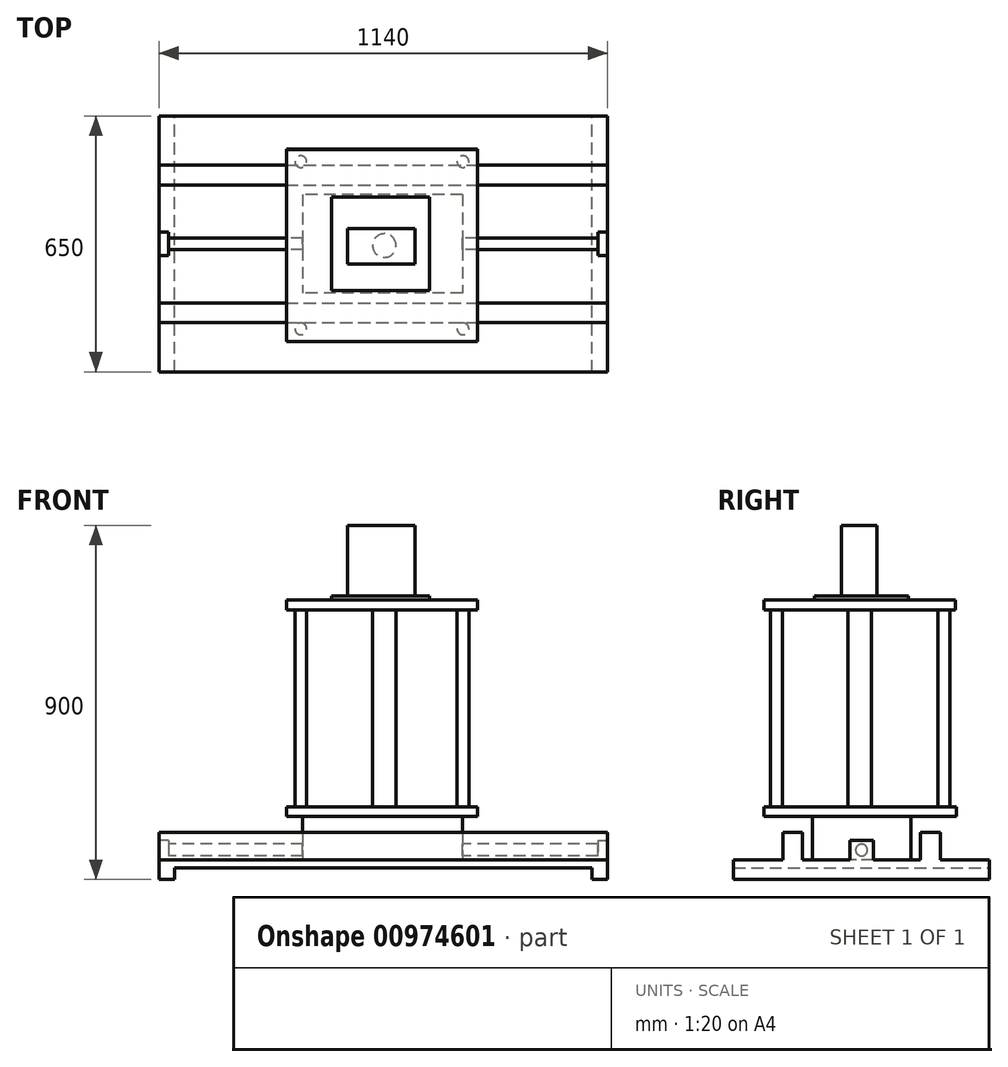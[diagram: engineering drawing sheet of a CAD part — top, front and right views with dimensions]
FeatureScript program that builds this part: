
annotation { "Feature Type Name" : "Feature", "Feature Type Description" : "" }
export const myFeature = defineFeature(function(context is Context, id is Id, definition is map)
    precondition{}
    {
        {
            var Q0;
            Q0=qCreatedBy(makeId("Front.planeOp"),FACE);
            var sketch = newSketch(context, id + "F0", { "sketchPlane" : qUnion([Q0])});
            skLineSegment(sketch, "E0", {"start": v(-162.63, 0) * mm, "end": v(-162.63, 50) * mm});
            skLineSegment(sketch, "E1", {"start": v(-162.63, 50) * mm, "end": v(977.37, 50) * mm});
            skLineSegment(sketch, "E2", {"start": v(977.37, 50) * mm, "end": v(977.37, 0) * mm});
            skLineSegment(sketch, "E3", {"start": v(977.37, 0) * mm, "end": v(937.37, 0) * mm});
            skLineSegment(sketch, "E4", {"start": v(937.37, 0) * mm, "end": v(937.37, 30) * mm});
            skLineSegment(sketch, "E5", {"start": v(937.37, 30) * mm, "end": v(-122.63, 30) * mm});
            skLineSegment(sketch, "E6", {"start": v(-122.63, 30) * mm, "end": v(-122.63, 0) * mm});
            skLineSegment(sketch, "E7", {"start": v(-122.63, 0) * mm, "end": v(-162.63, 0) * mm});
            skSolve(sketch);
        }
        {
            var Q0;
            Q0 = qSketchRegion(id + "F0", true);
            extrude(context, id + "F1", {"entities" : qUnion([Q0]), "depth" : 650 * mm, "offsetDistance" : 25 * mm});
        }
        {
            var Q0;
            Q0=makeQuery(id+"F1.opExtrude","SWEPT_FACE",FACE,{"disambiguationData":[OSD([sQuery(id+"F0.wireOp",EDGE,"E0")])]});
            var sketch = newSketch(context, id + "F2", { "sketchPlane" : qUnion([Q0])});
            skLineSegment(sketch, "E8.bottom", {"start": v(295, 100) * mm, "end": v(355, 100) * mm});
            skLineSegment(sketch, "E8.top", {"start": v(295, 50) * mm, "end": v(355, 50) * mm});
            skLineSegment(sketch, "E8.left", {"start": v(295, 100) * mm, "end": v(295, 50) * mm});
            skLineSegment(sketch, "E8.right", {"start": v(355, 100) * mm, "end": v(355, 50) * mm});
            skSolve(sketch);
        }
        {
            var Q0;
            Q0 = qSketchRegion(id + "F2", true);
            extrude(context, id + "F3", {"entities" : qUnion([Q0]), "oppositeDirection" : true, "depth" : 25 * mm, "offsetDistance" : 25 * mm});
        }
        {
            var Q0;
            Q0=makeQuery(id+"F1.opExtrude","SWEPT_FACE",FACE,{"disambiguationData":[OSD([sQuery(id+"F0.wireOp",EDGE,"E0")])]});
            cPlane(context, id + "F4", {"entities" : qUnion([Q0]), "cplaneType" : CPlaneType.OFFSET, "offset" : 570 * mm, "oppositeDirection" : true, "width" : 150 * mm, "height" : 150 * mm});
        }
        {
            var Q0;
            Q0=makeQuery(id+"F3.opExtrude","SWEPT_BODY",BODY,{"disambiguationData":[OSD([sQuery(id+"F2.wireOp",EDGE,"E8.bottom"),sQuery(id+"F2.wireOp",EDGE,"E8.top"),sQuery(id+"F2.wireOp",EDGE,"E8.left"),sQuery(id+"F2.wireOp",EDGE,"E8.right")])]});
            var Q1;
            Q1=qCreatedBy(id+"F4.planeOp",FACE);
            mirror(context, id + "F5", {"operationType" : NewBodyOperationType.ADD, "entities" : qUnion([Q0]), "mirrorPlane" : qUnion([Q1])});
        }
        {
            var Q0;
            Q0=makeQuery(id+"F3.opExtrude","CAP_FACE",FACE,{"disambiguationData":[OSD([sQuery(id+"F2.wireOp",EDGE,"E8.bottom"),sQuery(id+"F2.wireOp",EDGE,"E8.top"),sQuery(id+"F2.wireOp",EDGE,"E8.left"),sQuery(id+"F2.wireOp",EDGE,"E8.right")])],"isStart":false});
            var sketch = newSketch(context, id + "F6", { "sketchPlane" : qUnion([Q0])});
            skCircle(sketch, "E9", {"center": v(-325, 75) * mm, "radius": 15 * mm});
            skSolve(sketch);
        }
        {
            var Q0;
            Q0 = qSketchRegion(id + "F6", true);
            var Q1;
            Q1=makeQuery(id+"F5.opPattern","COPY",FACE,{"derivedFrom":makeQuery(id+"F3.opExtrude","CAP_FACE",FACE,{"disambiguationData":[OSD([sQuery(id+"F2.wireOp",EDGE,"E8.bottom"),sQuery(id+"F2.wireOp",EDGE,"E8.top"),sQuery(id+"F2.wireOp",EDGE,"E8.left"),sQuery(id+"F2.wireOp",EDGE,"E8.right")])],"isStart":false}),"instanceName":"1"});
            extrude(context, id + "F7", {"entities" : qUnion([Q0]), "operationType" : NewBodyOperationType.ADD, "endBound" : BoundingType.UP_TO_SURFACE, "depth" : 572 * mm, "endBoundEntityFace" : qUnion([Q1]), "offsetDistance" : 25 * mm});
        }
        {
            var Q0;
            Q0=makeQuery(id+"F1.opExtrude","SWEPT_FACE",FACE,{"disambiguationData":[OSD([sQuery(id+"F0.wireOp",EDGE,"E1")])]});
            var sketch = newSketch(context, id + "F8", { "sketchPlane" : qUnion([Q0])});
            skLineSegment(sketch, "E10.bottom", {"start": v(-162.63, -125) * mm, "end": v(977.37, -125) * mm});
            skLineSegment(sketch, "E10.top", {"start": v(-162.63, -175) * mm, "end": v(977.37, -175) * mm});
            skLineSegment(sketch, "E10.left", {"start": v(-162.63, -125) * mm, "end": v(-162.63, -175) * mm});
            skLineSegment(sketch, "E10.right", {"start": v(977.37, -125) * mm, "end": v(977.37, -175) * mm});
            skLineSegment(sketch, "E11.bottom", {"start": v(-162.63, -475) * mm, "end": v(977.37, -475) * mm});
            skLineSegment(sketch, "E11.top", {"start": v(-162.63, -525) * mm, "end": v(977.37, -525) * mm});
            skLineSegment(sketch, "E11.left", {"start": v(-162.63, -475) * mm, "end": v(-162.63, -525) * mm});
            skLineSegment(sketch, "E11.right", {"start": v(977.37, -475) * mm, "end": v(977.37, -525) * mm});
            skSolve(sketch);
        }
        {
            var Q0;
            Q0 = qSketchRegion(id + "F8", true);
            extrude(context, id + "F9", {"entities" : qUnion([Q0]), "operationType" : NewBodyOperationType.ADD, "depth" : 70 * mm, "offsetDistance" : 25 * mm});
        }
        {
            var Q0;
            {var subQ1=sQuery(id+"F2.wireOp",EDGE,"E8.left");var subQ6=makeQuery(id+"F3.opExtrude","SWEPT_FACE",FACE,{"disambiguationData":[OSD([subQ1])]});Q0=makeQuery(id+"F9.boolean.opBoolean","SPLIT",FACE,{"disambiguationData":[TD([subQ6])],"derivedFrom":makeQuery(id+"F1.opExtrude","SWEPT_FACE",FACE,{"disambiguationData":[OSD([sQuery(id+"F0.wireOp",EDGE,"E1")])]})});}
            var sketch = newSketch(context, id + "F10", { "sketchPlane" : qUnion([Q0])});
            skLineSegment(sketch, "E12.bottom", {"start": v(608.43, -199.48) * mm, "end": v(202.91, -199.48) * mm});
            skLineSegment(sketch, "E12.top", {"start": v(608.43, -449.38) * mm, "end": v(202.91, -449.38) * mm});
            skLineSegment(sketch, "E12.left", {"start": v(608.43, -199.48) * mm, "end": v(608.43, -449.38) * mm});
            skLineSegment(sketch, "E12.right", {"start": v(202.91, -199.48) * mm, "end": v(202.91, -449.38) * mm});
            skSolve(sketch);
        }
        {
            var Q0;
            Q0 = qSketchRegion(id + "F10", true);
            extrude(context, id + "F11", {"entities" : qUnion([Q0]), "operationType" : NewBodyOperationType.ADD, "depth" : 110 * mm, "offsetDistance" : 25 * mm});
        }
        {
            var Q0;
            Q0=makeQuery(id+"F11.opExtrude","CAP_FACE",FACE,{"disambiguationData":[OSD([sQuery(id+"F10.wireOp",EDGE,"E12.bottom"),sQuery(id+"F10.wireOp",EDGE,"E12.top"),sQuery(id+"F10.wireOp",EDGE,"E12.left"),sQuery(id+"F10.wireOp",EDGE,"E12.right")])],"isStart":false});
            var sketch = newSketch(context, id + "F12", { "sketchPlane" : qUnion([Q0])});
            skLineSegment(sketch, "E13.bottom", {"start": v(646.37, -83.98) * mm, "end": v(161.14, -83.98) * mm});
            skLineSegment(sketch, "E13.top", {"start": v(646.37, -572.94) * mm, "end": v(161.14, -572.94) * mm});
            skLineSegment(sketch, "E13.left", {"start": v(646.37, -83.98) * mm, "end": v(646.37, -572.94) * mm});
            skLineSegment(sketch, "E13.right", {"start": v(161.14, -83.98) * mm, "end": v(161.14, -572.94) * mm});
            skSolve(sketch);
        }
        {
            var Q0;
            Q0 = qSketchRegion(id + "F12", true);
            extrude(context, id + "F13", {"entities" : qUnion([Q0]), "depth" : 25 * mm, "offsetDistance" : 25 * mm});
        }
        {
            var Q0;
            Q0=makeQuery(id+"F13.opExtrude","CAP_FACE",FACE,{"disambiguationData":[OSD([sQuery(id+"F12.wireOp",EDGE,"E13.bottom"),sQuery(id+"F12.wireOp",EDGE,"E13.top"),sQuery(id+"F12.wireOp",EDGE,"E13.left"),sQuery(id+"F12.wireOp",EDGE,"E13.right")])],"isStart":false});
            var sketch = newSketch(context, id + "F14", { "sketchPlane" : qUnion([Q0])});
            skCircle(sketch, "E14", {"center": v(410.19, -329.26) * mm, "radius": 30 * mm});
            skSolve(sketch);
        }
        {
            var Q0;
            Q0 = qSketchRegion(id + "F14", true);
            extrude(context, id + "F15", {"entities" : qUnion([Q0]), "operationType" : NewBodyOperationType.ADD, "depth" : 500 * mm, "offsetDistance" : 25 * mm});
        }
        {
            var Q0;
            Q0=makeQuery(id+"F15.opExtrude","CAP_FACE",FACE,{"disambiguationData":[OSD([sQuery(id+"F14.wireOp",EDGE,"E14")])],"isStart":false});
            var sketch = newSketch(context, id + "F16", { "sketchPlane" : qUnion([Q0])});
            skLineSegment(sketch, "E15.bottom", {"start": v(646.33, -85.89) * mm, "end": v(161.2, -85.89) * mm});
            skLineSegment(sketch, "E15.top", {"start": v(646.33, -572.63) * mm, "end": v(161.2, -572.63) * mm});
            skLineSegment(sketch, "E15.left", {"start": v(646.33, -85.89) * mm, "end": v(646.33, -572.63) * mm});
            skLineSegment(sketch, "E15.right", {"start": v(161.2, -85.89) * mm, "end": v(161.2, -572.63) * mm});
            skSolve(sketch);
        }
        {
            var Q0;
            Q0 = qSketchRegion(id + "F16", true);
            extrude(context, id + "F17", {"entities" : qUnion([Q0]), "operationType" : NewBodyOperationType.ADD, "depth" : 25 * mm, "offsetDistance" : 25 * mm});
        }
        {
            var Q0;
            Q0=makeQuery(id+"F13.opExtrude","CAP_FACE",FACE,{"disambiguationData":[OSD([sQuery(id+"F12.wireOp",EDGE,"E13.bottom"),sQuery(id+"F12.wireOp",EDGE,"E13.top"),sQuery(id+"F12.wireOp",EDGE,"E13.left"),sQuery(id+"F12.wireOp",EDGE,"E13.right")])],"isStart":false});
            var sketch = newSketch(context, id + "F18", { "sketchPlane" : qUnion([Q0])});
            skCircle(sketch, "E16", {"center": v(197.7, -116.03) * mm, "radius": 15 * mm});
            skCircle(sketch, "E17.MirrorC", {"center": v(609.81, -116.03) * mm, "radius": 15 * mm});
            skCircle(sketch, "E18.MirrorC", {"center": v(197.7, -540.88) * mm, "radius": 15 * mm});
            skCircle(sketch, "E19.MirrorC", {"center": v(609.81, -540.88) * mm, "radius": 15 * mm});
            skSolve(sketch);
        }
        {
            var Q0;
            Q0 = qSketchRegion(id + "F18", true);
            var Q1;
            Q1=makeQuery(id+"F17.opExtrude","CAP_FACE",FACE,{"disambiguationData":[OSD([sQuery(id+"F16.wireOp",EDGE,"E15.bottom"),sQuery(id+"F16.wireOp",EDGE,"E15.top"),sQuery(id+"F16.wireOp",EDGE,"E15.left"),sQuery(id+"F16.wireOp",EDGE,"E15.right")])],"isStart":true});
            extrude(context, id + "F19", {"entities" : qUnion([Q0]), "operationType" : NewBodyOperationType.ADD, "endBound" : BoundingType.UP_TO_SURFACE, "depth" : 25 * mm, "endBoundEntityFace" : qUnion([Q1]), "offsetDistance" : 25 * mm});
        }
        {
            var Q0;
            Q0=makeQuery(id+"F17.opExtrude","CAP_FACE",FACE,{"disambiguationData":[OSD([sQuery(id+"F16.wireOp",EDGE,"E15.bottom"),sQuery(id+"F16.wireOp",EDGE,"E15.top"),sQuery(id+"F16.wireOp",EDGE,"E15.left"),sQuery(id+"F16.wireOp",EDGE,"E15.right")])],"isStart":false});
            var sketch = newSketch(context, id + "F20", { "sketchPlane" : qUnion([Q0])});
            skLineSegment(sketch, "E20.bottom", {"start": v(524.84, -443.97) * mm, "end": v(275.6, -443.97) * mm});
            skLineSegment(sketch, "E20.top", {"start": v(524.84, -206.06) * mm, "end": v(275.6, -206.06) * mm});
            skLineSegment(sketch, "E20.left", {"start": v(524.84, -443.97) * mm, "end": v(524.84, -206.06) * mm});
            skLineSegment(sketch, "E20.right", {"start": v(275.6, -443.97) * mm, "end": v(275.6, -206.06) * mm});
            skSolve(sketch);
        }
        {
            var Q0;
            Q0 = qSketchRegion(id + "F20", true);
            extrude(context, id + "F21", {"entities" : qUnion([Q0]), "operationType" : NewBodyOperationType.ADD, "depth" : 10 * mm, "offsetDistance" : 25 * mm});
        }
        {
            var Q0;
            Q0=makeQuery(id+"F21.opExtrude","CAP_FACE",FACE,{"disambiguationData":[OSD([sQuery(id+"F20.wireOp",EDGE,"E20.bottom"),sQuery(id+"F20.wireOp",EDGE,"E20.top"),sQuery(id+"F20.wireOp",EDGE,"E20.left"),sQuery(id+"F20.wireOp",EDGE,"E20.right")])],"isStart":false});
            var sketch = newSketch(context, id + "F22", { "sketchPlane" : qUnion([Q0])});
            skLineSegment(sketch, "E21.bottom", {"start": v(316.83, -286.52) * mm, "end": v(487.89, -286.52) * mm});
            skLineSegment(sketch, "E21.top", {"start": v(316.83, -376.33) * mm, "end": v(487.89, -376.33) * mm});
            skLineSegment(sketch, "E21.left", {"start": v(316.83, -286.52) * mm, "end": v(316.83, -376.33) * mm});
            skLineSegment(sketch, "E21.right", {"start": v(487.89, -286.52) * mm, "end": v(487.89, -376.33) * mm});
            skSolve(sketch);
        }
        {
            var Q0;
            Q0 = qSketchRegion(id + "F22", true);
            extrude(context, id + "F23", {"entities" : qUnion([Q0]), "depth" : 180 * mm, "offsetDistance" : 25 * mm});
        }
    });
